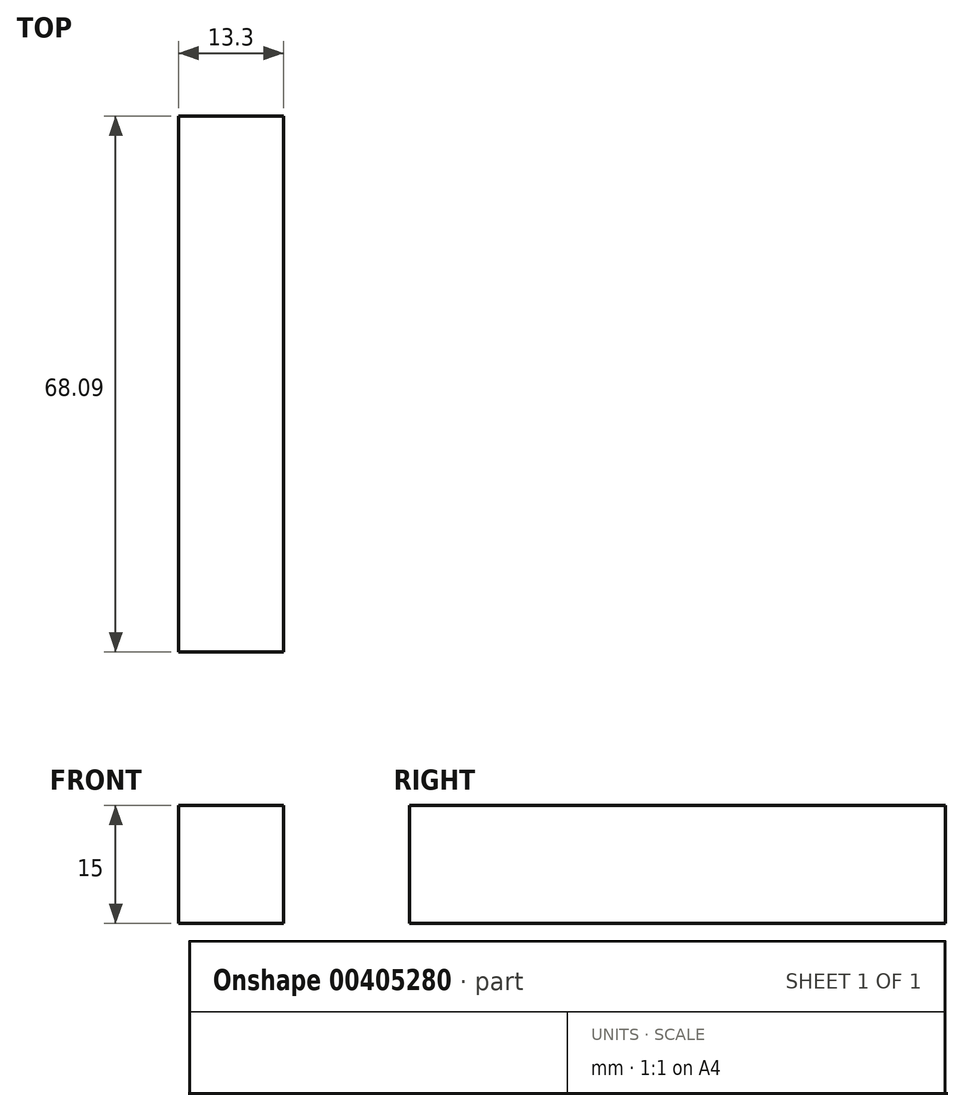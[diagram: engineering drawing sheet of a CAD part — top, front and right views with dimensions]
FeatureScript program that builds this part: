
annotation { "Feature Type Name" : "Feature", "Feature Type Description" : "" }
export const myFeature = defineFeature(function(context is Context, id is Id, definition is map)
    precondition{}
    {
        {
            var Q0;
            Q0=qCreatedBy(makeId("Top.planeOp"),FACE);
            var sketch = newSketch(context, id + "F0", { "sketchPlane" : qUnion([Q0])});
            skLineSegment(sketch, "E0.bottom", {"start": v(28.92, 47.35) * mm, "end": v(15.62, 47.35) * mm});
            skLineSegment(sketch, "E0.top", {"start": v(28.92, -20.74) * mm, "end": v(15.62, -20.74) * mm});
            skLineSegment(sketch, "E0.left", {"start": v(28.92, 47.35) * mm, "end": v(28.92, -20.74) * mm});
            skLineSegment(sketch, "E0.right", {"start": v(15.62, 47.35) * mm, "end": v(15.62, -20.74) * mm});
            skSolve(sketch);
        }
        {
            var Q0;
            Q0 = qSketchRegion(id + "F0", true);
            extrude(context, id + "F1", {"entities" : qUnion([Q0]), "depth" : 15 * mm});
        }
    });
